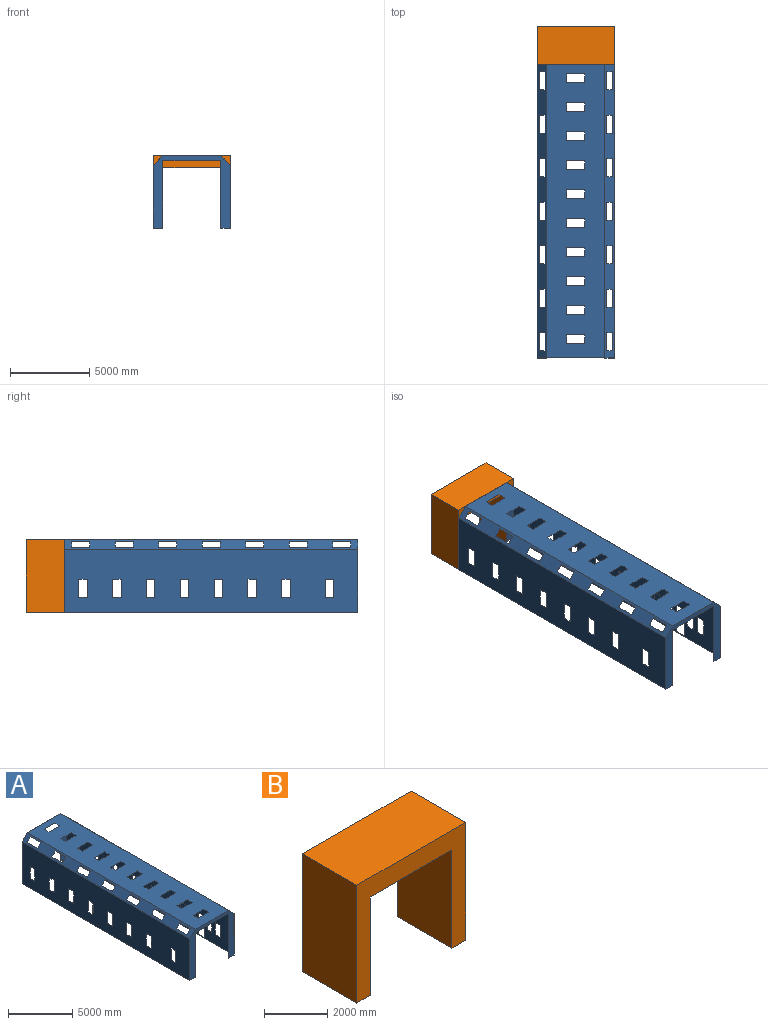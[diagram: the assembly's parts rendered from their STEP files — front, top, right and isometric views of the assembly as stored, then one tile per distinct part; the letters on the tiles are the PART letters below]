
ASSEMBLY  parts=2 mates=1
PART A: 200 faces, bbox 4902.2x18491.2x4572 mm
  f0: plane 18491.2x3962.4mm, normal (1,0,0), area 65012386.1mm2, adj f6,f11,f12,f15,f22,f23,f24,f121
  f1: plane 18485.1x3961.14mm, normal (-1,0,0), area 66186568.4mm2, adj f7,f13,f14,f15,f22,f23,f24,f121
  f2: plane 18491.2x3962.4mm, normal (-1,0,0), area 68392121.3mm2, adj f4,f10,f11,f12,f122,f123,f124,f125
  f3: plane 18485.1x3961.14mm, normal (1,0,0), area 68344628.6mm2, adj f5,f10,f13,f14,f122,f123,f124,f125
  f4: plane 18491.2x609.6mm, normal (-0.71,0,0.71), area 11673614.9mm2, adj f2,f8,f11,f12,f93,f94,f95,f96
  f5: plane 18485.1x607.81mm, normal (0.71,0,-0.71), area 11621683.8mm2, adj f3,f9,f13,f14,f93,f94,f95,f96
  f6: plane 18491.2x609.6mm, normal (0.71,0,0.71), area 11673614.9mm2, adj f0,f8,f11,f12,f65,f66,f67,f68
  f7: plane 18485.1x607.81mm, normal (-0.71,0,-0.71), area 11621683.8mm2, adj f1,f9,f13,f14,f65,f66,f67,f68
  f8: plane 18491.2x3657.6mm, normal (0,0,1), area 61536651.1mm2, adj f4,f6,f11,f12,f25,f26,f27,f28
  f9: plane 18485.1x3655.08mm, normal (0,0,-1), area 61467678.7mm2, adj f5,f7,f13,f14,f25,f26,f27,f28
  f10: plane 18491.2x609.6mm, normal (0,0,-1), area 60058.7mm2, adj f2,f3,f11,f12,f13,f14,f18,f19
  f11: plane 4876.8x4572mm, normal (0,-1,0), area 6317406.7mm2, adj f0,f2,f4,f6,f8,f10,f15,f19
  f12: plane 4876.8x4572mm, normal (0,1,0), area 6317406.7mm2, adj f0,f2,f4,f6,f8,f10,f15,f16
  f13: plane 4870.7x4568.95mm, normal (0,1,0), area 6276863.6mm2, adj f1,f3,f5,f7,f9,f10,f15,f19
  f14: plane 4870.7x4568.95mm, normal (0,-1,0), area 6276863.6mm2, adj f1,f3,f5,f7,f9,f10,f15,f16
  f15: plane 18491.2x609.6mm, normal (0,0,-1), area 60058.7mm2, adj f0,f1,f11,f12,f13,f14,f17,f20
  f16: plane 3657.6x3.05mm, normal (0,0,-1), area 11148.4mm2, adj f12,f14,f17,f18
  f17: plane 4267.2x3.05mm, normal (-1,0,0), area 13006.4mm2, adj f12,f14,f15,f16
  f18: plane 4267.2x3.05mm, normal (1,0,0), area 13006.4mm2, adj f10,f12,f14,f16
  f19: plane 4267.2x3.05mm, normal (1,0,0), area 13006.4mm2, adj f10,f11,f13,f21
  f20: plane 4267.2x3.05mm, normal (-1,0,0), area 13006.4mm2, adj f11,f13,f15,f21
  f21: plane 3657.6x3.05mm, normal (0,0,-1), area 11148.4mm2, adj f11,f13,f19,f20
  f22: plane 2035.05x3.05mm, normal (0,1,0), area 6198.2mm2, adj f0,f1,f24,f121
  f23: plane 2035.05x3.05mm, normal (0,-1,0), area 6198.2mm2, adj f0,f1,f24,f121
  f24: plane 762x3.05mm, normal (0,0,-1), area 2322.6mm2, adj f0,f1,f22,f23
  f25: plane 533.4x3.05mm, normal (1,0,0), area 1625.8mm2, adj f8,f9,f26,f28
  f26: plane 1143x3.05mm, normal (0,1,0), area 3483.9mm2, adj f8,f9,f25,f27
  f27: plane 533.4x3.05mm, normal (-1,0,0), area 1625.8mm2, adj f8,f9,f26,f28
  f28: plane 1143x3.05mm, normal (0,-1,0), area 3483.9mm2, adj f8,f9,f25,f27
  f29: plane 533.4x3.05mm, normal (1,0,0), area 1625.8mm2, adj f8,f9,f30,f32
  f30: plane 1143x3.05mm, normal (0,1,0), area 3483.9mm2, adj f8,f9,f29,f31
  f31: plane 533.4x3.05mm, normal (-1,0,0), area 1625.8mm2, adj f8,f9,f30,f32
  f32: plane 1143x3.05mm, normal (0,-1,0), area 3483.9mm2, adj f8,f9,f29,f31
  f33: plane 533.4x3.05mm, normal (1,0,0), area 1625.8mm2, adj f8,f9,f34,f36
  f34: plane 1143x3.05mm, normal (0,1,0), area 3483.9mm2, adj f8,f9,f33,f35
  f35: plane 533.4x3.05mm, normal (-1,0,0), area 1625.8mm2, adj f8,f9,f34,f36
  f36: plane 1143x3.05mm, normal (0,-1,0), area 3483.9mm2, adj f8,f9,f33,f35
  f37: plane 533.4x3.05mm, normal (1,0,0), area 1625.8mm2, adj f8,f9,f38,f40
  f38: plane 1143x3.05mm, normal (0,1,0), area 3483.9mm2, adj f8,f9,f37,f39
  f39: plane 533.4x3.05mm, normal (-1,0,0), area 1625.8mm2, adj f8,f9,f38,f40
  f40: plane 1143x3.05mm, normal (0,-1,0), area 3483.9mm2, adj f8,f9,f37,f39
  f41: plane 533.4x3.05mm, normal (1,0,0), area 1625.8mm2, adj f8,f9,f42,f44
  f42: plane 1143x3.05mm, normal (0,1,0), area 3483.9mm2, adj f8,f9,f41,f43
  f43: plane 533.4x3.05mm, normal (-1,0,0), area 1625.8mm2, adj f8,f9,f42,f44
  f44: plane 1143x3.05mm, normal (0,-1,0), area 3483.9mm2, adj f8,f9,f41,f43
  f45: plane 533.4x3.05mm, normal (1,0,0), area 1625.8mm2, adj f8,f9,f46,f48
  f46: plane 1143x3.05mm, normal (0,1,0), area 3483.9mm2, adj f8,f9,f45,f47
  f47: plane 533.4x3.05mm, normal (-1,0,0), area 1625.8mm2, adj f8,f9,f46,f48
  f48: plane 1143x3.05mm, normal (0,-1,0), area 3483.9mm2, adj f8,f9,f45,f47
  f49: plane 533.4x3.05mm, normal (1,0,0), area 1625.8mm2, adj f8,f9,f50,f52
  f50: plane 1143x3.05mm, normal (0,1,0), area 3483.9mm2, adj f8,f9,f49,f51
  f51: plane 533.4x3.05mm, normal (-1,0,0), area 1625.8mm2, adj f8,f9,f50,f52
  f52: plane 1143x3.05mm, normal (0,-1,0), area 3483.9mm2, adj f8,f9,f49,f51
  f53: plane 533.4x3.05mm, normal (1,0,0), area 1625.8mm2, adj f8,f9,f54,f56
  f54: plane 1143x3.05mm, normal (0,1,0), area 3483.9mm2, adj f8,f9,f53,f55
  f55: plane 533.4x3.05mm, normal (-1,0,0), area 1625.8mm2, adj f8,f9,f54,f56
  f56: plane 1143x3.05mm, normal (0,-1,0), area 3483.9mm2, adj f8,f9,f53,f55
  f57: plane 533.4x3.05mm, normal (1,0,0), area 1625.8mm2, adj f8,f9,f58,f60
  f58: plane 1143x3.05mm, normal (0,1,0), area 3483.9mm2, adj f8,f9,f57,f59
  f59: plane 533.4x3.05mm, normal (-1,0,0), area 1625.8mm2, adj f8,f9,f58,f60
  f60: plane 1143x3.05mm, normal (0,-1,0), area 3483.9mm2, adj f8,f9,f57,f59
  f61: plane 533.4x3.05mm, normal (1,0,0), area 1625.8mm2, adj f8,f9,f62,f64
  f62: plane 1143x3.05mm, normal (0,1,0), area 3483.9mm2, adj f8,f9,f61,f63
  f63: plane 533.4x3.05mm, normal (-1,0,0), area 1625.8mm2, adj f8,f9,f62,f64
  f64: plane 1143x3.05mm, normal (0,-1,0), area 3483.9mm2, adj f8,f9,f61,f63
  f65: plane 1143x2.16mm, normal (0.71,0,-0.71), area 3483.9mm2, adj f6,f7,f66,f68
  f66: plane 379.33x379.33mm, normal (0,1,0), area 1625.8mm2, adj f6,f7,f65,f67
  f67: plane 1143x2.16mm, normal (-0.71,0,0.71), area 3483.9mm2, adj f6,f7,f66,f68
  f68: plane 379.33x379.33mm, normal (0,-1,0), area 1625.8mm2, adj f6,f7,f65,f67
  f69: plane 1143x2.16mm, normal (0.71,0,-0.71), area 3483.9mm2, adj f6,f7,f70,f72
  f70: plane 379.33x379.33mm, normal (0,1,0), area 1625.8mm2, adj f6,f7,f69,f71
  f71: plane 1143x2.16mm, normal (-0.71,0,0.71), area 3483.9mm2, adj f6,f7,f70,f72
  f72: plane 379.33x379.33mm, normal (0,-1,0), area 1625.8mm2, adj f6,f7,f69,f71
  f73: plane 1143x2.16mm, normal (0.71,0,-0.71), area 3483.9mm2, adj f6,f7,f74,f76
  f74: plane 379.33x379.33mm, normal (0,1,0), area 1625.8mm2, adj f6,f7,f73,f75
  f75: plane 1143x2.16mm, normal (-0.71,0,0.71), area 3483.9mm2, adj f6,f7,f74,f76
  f76: plane 379.33x379.33mm, normal (0,-1,0), area 1625.8mm2, adj f6,f7,f73,f75
  f77: plane 1143x2.16mm, normal (0.71,0,-0.71), area 3483.9mm2, adj f6,f7,f78,f80
  f78: plane 379.33x379.33mm, normal (0,1,0), area 1625.8mm2, adj f6,f7,f77,f79
  f79: plane 1143x2.16mm, normal (-0.71,0,0.71), area 3483.9mm2, adj f6,f7,f78,f80
  f80: plane 379.33x379.33mm, normal (0,-1,0), area 1625.8mm2, adj f6,f7,f77,f79
  f81: plane 1143x2.16mm, normal (0.71,0,-0.71), area 3483.9mm2, adj f6,f7,f82,f84
  f82: plane 379.33x379.33mm, normal (0,1,0), area 1625.8mm2, adj f6,f7,f81,f83
  f83: plane 1143x2.16mm, normal (-0.71,0,0.71), area 3483.9mm2, adj f6,f7,f82,f84
  f84: plane 379.33x379.33mm, normal (0,-1,0), area 1625.8mm2, adj f6,f7,f81,f83
  f85: plane 1143x2.16mm, normal (0.71,0,-0.71), area 3483.9mm2, adj f6,f7,f86,f88
  f86: plane 379.33x379.33mm, normal (0,1,0), area 1625.8mm2, adj f6,f7,f85,f87
  f87: plane 1143x2.16mm, normal (-0.71,0,0.71), area 3483.9mm2, adj f6,f7,f86,f88
  f88: plane 379.33x379.33mm, normal (0,-1,0), area 1625.8mm2, adj f6,f7,f85,f87
  f89: plane 1143x2.16mm, normal (0.71,0,-0.71), area 3483.9mm2, adj f6,f7,f90,f92
  f90: plane 379.33x379.33mm, normal (0,1,0), area 1625.8mm2, adj f6,f7,f89,f91
  f91: plane 1143x2.16mm, normal (-0.71,0,0.71), area 3483.9mm2, adj f6,f7,f90,f92
  f92: plane 379.33x379.33mm, normal (0,-1,0), area 1625.8mm2, adj f6,f7,f89,f91
  f93: plane 379.33x379.33mm, normal (0,1,0), area 1625.8mm2, adj f4,f5,f94,f96
  f94: plane 1143x2.16mm, normal (-0.71,0,-0.71), area 3483.9mm2, adj f4,f5,f93,f95
  f95: plane 379.33x379.33mm, normal (0,-1,0), area 1625.8mm2, adj f4,f5,f94,f96
  f96: plane 1143x2.16mm, normal (0.71,0,0.71), area 3483.9mm2, adj f4,f5,f93,f95
  f97: plane 379.33x379.33mm, normal (0,1,0), area 1625.8mm2, adj f4,f5,f98,f100
  f98: plane 1143x2.16mm, normal (-0.71,0,-0.71), area 3483.9mm2, adj f4,f5,f97,f99
  f99: plane 379.33x379.33mm, normal (0,-1,0), area 1625.8mm2, adj f4,f5,f98,f100
  f100: plane 1143x2.16mm, normal (0.71,0,0.71), area 3483.9mm2, adj f4,f5,f97,f99
  f101: plane 379.33x379.33mm, normal (0,1,0), area 1625.8mm2, adj f4,f5,f102,f104
  f102: plane 1143x2.16mm, normal (-0.71,0,-0.71), area 3483.9mm2, adj f4,f5,f101,f103
  f103: plane 379.33x379.33mm, normal (0,-1,0), area 1625.8mm2, adj f4,f5,f102,f104
  f104: plane 1143x2.16mm, normal (0.71,0,0.71), area 3483.9mm2, adj f4,f5,f101,f103
  f105: plane 379.33x379.33mm, normal (0,1,0), area 1625.8mm2, adj f4,f5,f106,f108
  f106: plane 1143x2.16mm, normal (-0.71,0,-0.71), area 3483.9mm2, adj f4,f5,f105,f107
  f107: plane 379.33x379.33mm, normal (0,-1,0), area 1625.8mm2, adj f4,f5,f106,f108
  f108: plane 1143x2.16mm, normal (0.71,0,0.71), area 3483.9mm2, adj f4,f5,f105,f107
  f109: plane 379.33x379.33mm, normal (0,1,0), area 1625.8mm2, adj f4,f5,f110,f112
  f110: plane 1143x2.16mm, normal (-0.71,0,-0.71), area 3483.9mm2, adj f4,f5,f109,f111
  f111: plane 379.33x379.33mm, normal (0,-1,0), area 1625.8mm2, adj f4,f5,f110,f112
  f112: plane 1143x2.16mm, normal (0.71,0,0.71), area 3483.9mm2, adj f4,f5,f109,f111
  f113: plane 379.33x379.33mm, normal (0,1,0), area 1625.8mm2, adj f4,f5,f114,f116
  f114: plane 1143x2.16mm, normal (-0.71,0,-0.71), area 3483.9mm2, adj f4,f5,f113,f115
  f115: plane 379.33x379.33mm, normal (0,-1,0), area 1625.8mm2, adj f4,f5,f114,f116
  f116: plane 1143x2.16mm, normal (0.71,0,0.71), area 3483.9mm2, adj f4,f5,f113,f115
  f117: plane 379.33x379.33mm, normal (0,1,0), area 1625.8mm2, adj f4,f5,f118,f120
  f118: plane 1143x2.16mm, normal (-0.71,0,-0.71), area 3483.9mm2, adj f4,f5,f117,f119
  f119: plane 379.33x379.33mm, normal (0,-1,0), area 1625.8mm2, adj f4,f5,f118,f120
  f120: plane 1143x2.16mm, normal (0.71,0,0.71), area 3483.9mm2, adj f4,f5,f117,f119
  f121: plane 762x3.05mm, normal (0.71,0,0.71), area 3284.6mm2, adj f0,f1,f22,f23
  f122: plane 1143x3.05mm, normal (0,-1,0), area 3483.9mm2, adj f2,f3,f123,f125
  f123: plane 533.4x3.05mm, normal (0,0,1), area 1625.8mm2, adj f2,f3,f122,f124
  f124: plane 1143x3.05mm, normal (0,1,0), area 3483.9mm2, adj f2,f3,f123,f125
  f125: plane 533.4x3.05mm, normal (0,0,-1), area 1625.8mm2, adj f2,f3,f122,f124
  f126: plane 533.4x3.05mm, normal (0,0,-1), area 1625.8mm2, adj f0,f1,f127,f129
  f127: plane 1143x3.05mm, normal (0,1,0), area 3483.9mm2, adj f0,f1,f126,f128
  f128: plane 533.4x3.05mm, normal (0,0,1), area 1625.8mm2, adj f0,f1,f127,f129
  f129: plane 1143x3.05mm, normal (0,-1,0), area 3483.9mm2, adj f0,f1,f126,f128
  f130: plane 533.4x3.05mm, normal (0,0,-1), area 1625.8mm2, adj f0,f1,f131,f133
  f131: plane 1143x3.05mm, normal (0,1,0), area 3483.9mm2, adj f0,f1,f130,f132
  f132: plane 533.4x3.05mm, normal (0,0,1), area 1625.8mm2, adj f0,f1,f131,f133
  f133: plane 1143x3.05mm, normal (0,-1,0), area 3483.9mm2, adj f0,f1,f130,f132
  f134: plane 1143x3.05mm, normal (0,-1,0), area 3483.9mm2, adj f2,f3,f135,f137
  f135: plane 533.4x3.05mm, normal (0,0,1), area 1625.8mm2, adj f2,f3,f134,f136
  f136: plane 1143x3.05mm, normal (0,1,0), area 3483.9mm2, adj f2,f3,f135,f137
  f137: plane 533.4x3.05mm, normal (0,0,-1), area 1625.8mm2, adj f2,f3,f134,f136
  f138: plane 1143x3.05mm, normal (0,-1,0), area 3483.9mm2, adj f2,f3,f139,f141
  f139: plane 533.4x3.05mm, normal (0,0,1), area 1625.8mm2, adj f2,f3,f138,f140
  f140: plane 1143x3.05mm, normal (0,1,0), area 3483.9mm2, adj f2,f3,f139,f141
  f141: plane 533.4x3.05mm, normal (0,0,-1), area 1625.8mm2, adj f2,f3,f138,f140
  f142: plane 1143x3.05mm, normal (0,-1,0), area 3483.9mm2, adj f2,f3,f143,f145
  f143: plane 533.4x3.05mm, normal (0,0,1), area 1625.8mm2, adj f2,f3,f142,f144
  f144: plane 1143x3.05mm, normal (0,1,0), area 3483.9mm2, adj f2,f3,f143,f145
  f145: plane 533.4x3.05mm, normal (0,0,-1), area 1625.8mm2, adj f2,f3,f142,f144
  f146: plane 1143x3.05mm, normal (0,-1,0), area 3483.9mm2, adj f2,f3,f147,f149
  f147: plane 533.4x3.05mm, normal (0,0,1), area 1625.8mm2, adj f2,f3,f146,f148
  f148: plane 1143x3.05mm, normal (0,1,0), area 3483.9mm2, adj f2,f3,f147,f149
  f149: plane 533.4x3.05mm, normal (0,0,-1), area 1625.8mm2, adj f2,f3,f146,f148
  f150: plane 1143x3.05mm, normal (0,-1,0), area 3483.9mm2, adj f2,f3,f151,f153
  f151: plane 533.4x3.05mm, normal (0,0,1), area 1625.8mm2, adj f2,f3,f150,f152
  f152: plane 1143x3.05mm, normal (0,1,0), area 3483.9mm2, adj f2,f3,f151,f153
  f153: plane 533.4x3.05mm, normal (0,0,-1), area 1625.8mm2, adj f2,f3,f150,f152
  f154: plane 1143x3.05mm, normal (0,-1,0), area 3483.9mm2, adj f2,f3,f155,f157
  f155: plane 533.4x3.05mm, normal (0,0,1), area 1625.8mm2, adj f2,f3,f154,f156
  f156: plane 1143x3.05mm, normal (0,1,0), area 3483.9mm2, adj f2,f3,f155,f157
  f157: plane 533.4x3.05mm, normal (0,0,-1), area 1625.8mm2, adj f2,f3,f154,f156
  f158: plane 1143x3.05mm, normal (0,-1,0), area 3483.9mm2, adj f2,f3,f159,f161
  f159: plane 533.4x3.05mm, normal (0,0,1), area 1625.8mm2, adj f2,f3,f158,f160
  f160: plane 1143x3.05mm, normal (0,1,0), area 3483.9mm2, adj f2,f3,f159,f161
  f161: plane 533.4x3.05mm, normal (0,0,-1), area 1625.8mm2, adj f2,f3,f158,f160
  f162: plane 533.4x3.05mm, normal (0,0,-1), area 1625.8mm2, adj f0,f1,f163,f165
  f163: plane 1143x3.05mm, normal (0,1,0), area 3483.9mm2, adj f0,f1,f162,f164
  f164: plane 533.4x3.05mm, normal (0,0,1), area 1625.8mm2, adj f0,f1,f163,f165
  f165: plane 1143x3.05mm, normal (0,-1,0), area 3483.9mm2, adj f0,f1,f162,f164
  f166: plane 533.4x3.05mm, normal (0,0,-1), area 1625.8mm2, adj f0,f1,f167,f169
  f167: plane 1143x3.05mm, normal (0,1,0), area 3483.9mm2, adj f0,f1,f166,f168
  f168: plane 533.4x3.05mm, normal (0,0,1), area 1625.8mm2, adj f0,f1,f167,f169
  f169: plane 1143x3.05mm, normal (0,-1,0), area 3483.9mm2, adj f0,f1,f166,f168
  f170: plane 533.4x3.05mm, normal (0,0,-1), area 1625.8mm2, adj f0,f1,f171,f173
  f171: plane 1143x3.05mm, normal (0,1,0), area 3483.9mm2, adj f0,f1,f170,f172
  f172: plane 533.4x3.05mm, normal (0,0,1), area 1625.8mm2, adj f0,f1,f171,f173
  f173: plane 1143x3.05mm, normal (0,-1,0), area 3483.9mm2, adj f0,f1,f170,f172
  f174: plane 533.4x3.05mm, normal (0,0,-1), area 1625.8mm2, adj f0,f1,f175,f177
  f175: plane 1143x3.05mm, normal (0,1,0), area 3483.9mm2, adj f0,f1,f174,f176
  f176: plane 533.4x3.05mm, normal (0,0,1), area 1625.8mm2, adj f0,f1,f175,f177
  f177: plane 1143x3.05mm, normal (0,-1,0), area 3483.9mm2, adj f0,f1,f174,f176
  f178: plane 533.4x3.05mm, normal (0,0,-1), area 1625.8mm2, adj f0,f1,f179,f181
  f179: plane 1143x3.05mm, normal (0,1,0), area 3483.9mm2, adj f0,f1,f178,f180
  f180: plane 533.4x3.05mm, normal (0,0,1), area 1625.8mm2, adj f0,f1,f179,f181
  f181: plane 1143x3.05mm, normal (0,-1,0), area 3483.9mm2, adj f0,f1,f178,f180
  f182: plane 533.4x3.05mm, normal (0,0,-1), area 1625.8mm2, adj f0,f1,f183,f185
  f183: plane 1143x3.05mm, normal (0,1,0), area 3483.9mm2, adj f0,f1,f182,f184
  f184: plane 533.4x3.05mm, normal (0,0,1), area 1625.8mm2, adj f0,f1,f183,f185
  f185: plane 1143x3.05mm, normal (0,-1,0), area 3483.9mm2, adj f0,f1,f182,f184
  f186: plane 533.4x3.05mm, normal (0,0,-1), area 1625.8mm2, adj f0,f1,f187,f189
  f187: plane 1143x3.05mm, normal (0,1,0), area 3483.9mm2, adj f0,f1,f186,f188
  f188: plane 533.4x3.05mm, normal (0,0,1), area 1625.8mm2, adj f0,f1,f187,f189
  f189: plane 1143x3.05mm, normal (0,-1,0), area 3483.9mm2, adj f0,f1,f186,f188
  f190: plane 533.4x25.4mm, normal (0,0,1), area 13548.4mm2, adj f0,f191,f193,f194
  f191: plane 1143x25.4mm, normal (0,-1,0), area 29032.2mm2, adj f0,f190,f192,f194
  f192: plane 533.4x25.4mm, normal (0,0,-1), area 13548.4mm2, adj f0,f191,f193,f194
  f193: plane 1143x25.4mm, normal (0,1,0), area 29032.2mm2, adj f0,f190,f192,f194
  f194: plane 1143x533.4mm, normal (1,0,0), area 609676.2mm2, adj f190,f191,f192,f193
  f195: plane 533.4x25.4mm, normal (0,0,1), area 13548.4mm2, adj f0,f196,f198,f199
  f196: plane 1143x25.4mm, normal (0,-1,0), area 29032.2mm2, adj f0,f195,f197,f199
  f197: plane 533.4x25.4mm, normal (0,0,-1), area 13548.4mm2, adj f0,f196,f198,f199
  f198: plane 1143x25.4mm, normal (0,1,0), area 29032.2mm2, adj f0,f195,f197,f199
  f199: plane 1143x533.4mm, normal (1,0,0), area 609676.2mm2, adj f195,f196,f197,f198
PART B: 10 faces, bbox 4876.8x2438.4x4572 mm
  f0: plane 2438.4x609.6mm, normal (0,0,-1), area 1486448.6mm2, adj f1,f2,f5,f8
  f1: plane 4876.8x4572mm, normal (0,-1,0), area 8361273.6mm2, adj f0,f3,f4,f5,f6,f7,f8,f9
  f2: plane 4876.8x4572mm, normal (0,1,0), area 8361273.6mm2, adj f0,f3,f4,f5,f6,f7,f8,f9
  f3: plane 4572x2438.4mm, normal (-1,0,0), area 11148364.8mm2, adj f1,f2,f4,f6
  f4: plane 2438.4x609.6mm, normal (0,0,-1), area 1486448.6mm2, adj f1,f2,f3,f7
  f5: plane 4572x2438.4mm, normal (1,0,0), area 11148364.8mm2, adj f0,f1,f2,f6
  f6: plane 4876.8x2438.4mm, normal (0,0,1), area 11891589.1mm2, adj f1,f2,f3,f5
  f7: plane 3810x2438.4mm, normal (1,0,0), area 9290304mm2, adj f1,f2,f4,f9
  f8: plane 3810x2438.4mm, normal (-1,0,0), area 9290304mm2, adj f0,f1,f2,f9
  f9: plane 3657.6x2438.4mm, normal (0,0,-1), area 8918691.8mm2, adj f1,f2,f7,f8
PLACE A t=(-5609.07,-26506.66,-31507.03)mm
PLACE B t=(-5609.07,-24068.26,-31507.03)mm
MATE fastened A.f12 <-> B.f1  axis (0,1,0) through (-3170.67,-26506.66,-26935.03)mm
